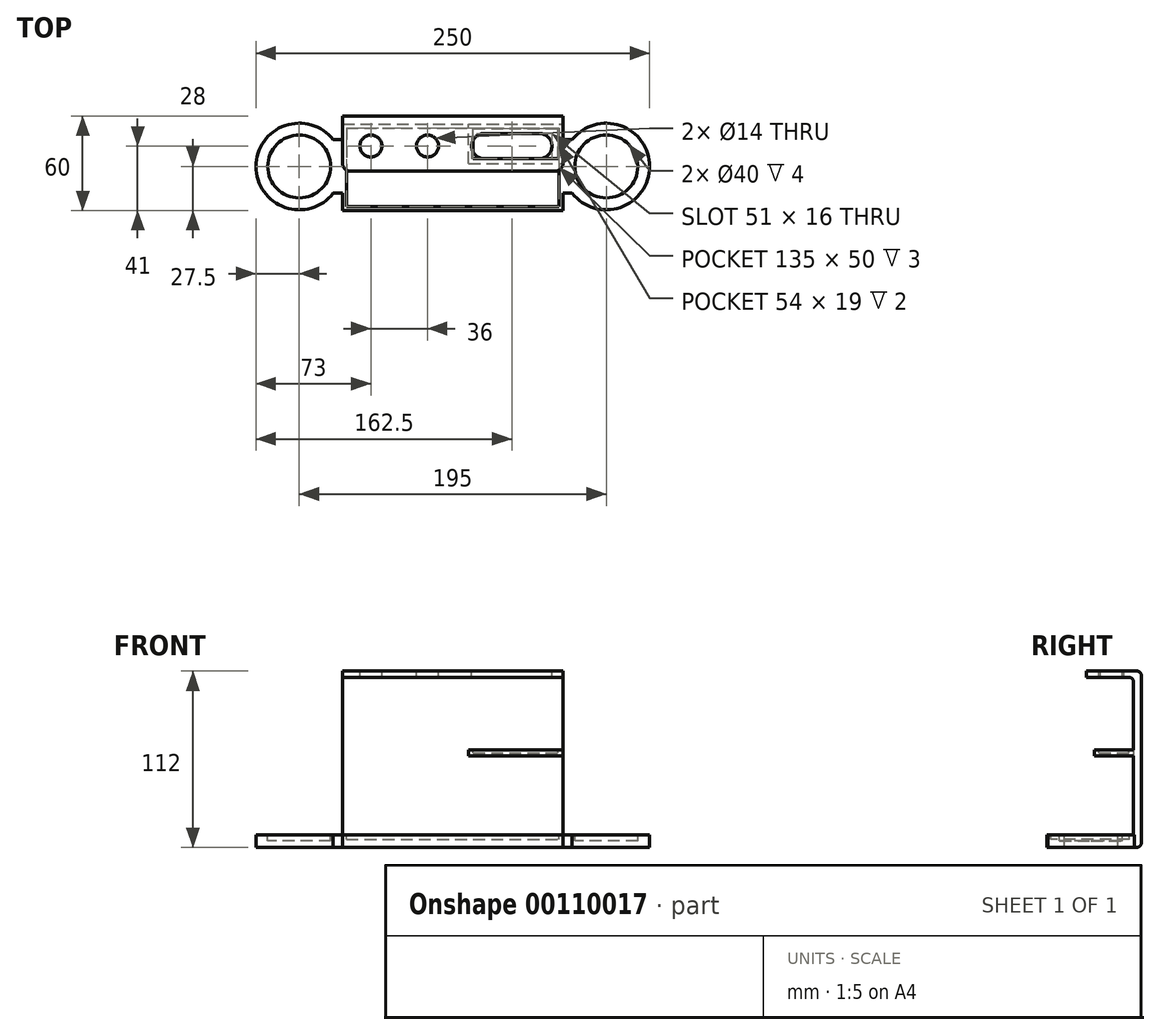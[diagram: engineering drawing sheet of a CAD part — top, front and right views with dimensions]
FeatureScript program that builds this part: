
annotation { "Feature Type Name" : "Feature", "Feature Type Description" : "" }
export const myFeature = defineFeature(function(context is Context, id is Id, definition is map)
    precondition{}
    {
        {
            var Q0;
            Q0=qCreatedBy(makeId("Right.planeOp"),FACE);
            var sketch = newSketch(context, id + "F0", { "sketchPlane" : qUnion([Q0])});
            skLineSegment(sketch, "E0", {"start": v(-85.22, 0) * mm, "end": v(92.32, 0) * mm, "construction": true});
            skLineSegment(sketch, "E1", {"start": v(0, 78) * mm, "end": v(0, -85.56) * mm, "construction": true});
            skLineSegment(sketch, "E2.right", {"start": v(0, 51) * mm, "end": v(0, -55) * mm});
            skLineSegment(sketch, "E3.top", {"start": v(-60, -50) * mm, "end": v(-5, -50) * mm});
            skLineSegment(sketch, "E3.right", {"start": v(-5, 47) * mm, "end": v(-5, -50) * mm});
            skLineSegment(sketch, "E4", {"start": v(-3, 54) * mm, "end": v(-35, 54) * mm});
            skLineSegment(sketch, "E5", {"start": v(-35, 50) * mm, "end": v(-8, 50) * mm});
            skLineSegment(sketch, "E6", {"start": v(-3, -58) * mm, "end": v(-60, -58) * mm});
            skLineSegment(sketch, "E7", {"start": v(-60, -50) * mm, "end": v(-60, -58) * mm});
            skPoint(sketch, "E8.visualSharp", {"position": v(0, 54) * mm});
            skArc(sketch, "E8.filletArc", {"start": v(0, 51) * mm, "mid": v(-0.88, 53.12) * mm, "end": v(-3, 54) * mm});
            skPoint(sketch, "E9.visualSharp", {"position": v(0, -58) * mm});
            skArc(sketch, "E9.filletArc", {"start": v(-3, -58) * mm, "mid": v(-0.88, -57.12) * mm, "end": v(0, -55) * mm});
            skPoint(sketch, "E10.visualSharp", {"position": v(-5, 50) * mm});
            skArc(sketch, "E10.filletArc", {"start": v(-5, 47) * mm, "mid": v(-5.88, 49.12) * mm, "end": v(-8, 50) * mm});
            skLineSegment(sketch, "E11", {"start": v(-35, 54) * mm, "end": v(-35, 50) * mm});
            skSolve(sketch);
        }
        {
            var Q0;
            Q0=makeQuery(id+"F0.imprint","IMPRINT",FACE,{"disambiguationData":[TD([[makeQuery(id+"F0.imprint","IMPRINT",EDGE,{"derivedFrom":sQuery(id+"F0.wireOp",EDGE,"E2.right")}),-1.0]])]});
            extrude(context, id + "F1", {"entities" : qUnion([Q0]), "oppositeDirection" : true, "depth" : 70 * mm, "hasSecondDirection" : true, "secondDirectionOppositeDirection" : false, "secondDirectionDepth" : 70 * mm});
        }
        {
            var Q0;
            Q0=makeQuery(id+"F1.opExtrude","SWEPT_FACE",FACE,{"disambiguationData":[OSD([sQuery(id+"F0.wireOp",EDGE,"E4")])]});
            var sketch = newSketch(context, id + "F2", { "sketchPlane" : qUnion([Q0])});
            skCircle(sketch, "E12", {"center": v(-52, -19) * mm, "radius": 7 * mm});
            skCircle(sketch, "E13", {"center": v(-16, -19) * mm, "radius": 7 * mm});
            skLineSegment(sketch, "E14", {"start": v(-78.22, -19) * mm, "end": v(92.14, -19) * mm, "construction": true});
            skLineSegment(sketch, "E15", {"start": v(0, 33.35) * mm, "end": v(0, -66.78) * mm, "construction": true});
            skArc(sketch, "E16", {"start": v(20, -11) * mm, "mid": v(12, -19) * mm, "end": v(20, -27) * mm});
            skArc(sketch, "E17", {"start": v(55, -27) * mm, "mid": v(63, -19) * mm, "end": v(55, -11) * mm});
            skLineSegment(sketch, "E18.bottom", {"start": v(20, -11) * mm, "end": v(55, -11) * mm});
            skLineSegment(sketch, "E18.top", {"start": v(20, -27) * mm, "end": v(55, -27) * mm});
            skSolve(sketch);
        }
        {
            var Q0;
            Q0=makeQuery(id+"F2.imprint","IMPRINT",FACE,{"disambiguationData":[TD([[makeQuery(id+"F2.imprint","IMPRINT",EDGE,{"derivedFrom":sQuery(id+"F2.wireOp",EDGE,"E16")}),1.0]])]});
            var Q1;
            Q1=makeQuery(id+"F2.imprint","IMPRINT",FACE,{"disambiguationData":[TD([[makeQuery(id+"F2.imprint","IMPRINT",EDGE,{"derivedFrom":sQuery(id+"F2.wireOp",EDGE,"E13")}),1.0]])]});
            var Q2;
            Q2=makeQuery(id+"F2.imprint","IMPRINT",FACE,{"disambiguationData":[TD([[makeQuery(id+"F2.imprint","IMPRINT",EDGE,{"derivedFrom":sQuery(id+"F2.wireOp",EDGE,"E12")}),1.0]])]});
            extrude(context, id + "F3", {"entities" : qUnion([Q0, Q1, Q2]), "operationType" : NewBodyOperationType.REMOVE, "endBound" : BoundingType.UP_TO_NEXT, "oppositeDirection" : true, "depth" : 25 * mm});
        }
        {
            var Q0;
            Q0=makeQuery(id+"F1.opExtrude","SWEPT_FACE",FACE,{"disambiguationData":[OSD([sQuery(id+"F0.wireOp",EDGE,"E3.top")])]});
            var sketch = newSketch(context, id + "F4", { "sketchPlane" : qUnion([Q0])});
            skLineSegment(sketch, "E19.bottom", {"start": v(-67.5, -7.5) * mm, "end": v(67.5, -7.5) * mm});
            skLineSegment(sketch, "E19.top", {"start": v(-67.5, -57.5) * mm, "end": v(67.5, -57.5) * mm});
            skLineSegment(sketch, "E19.left", {"start": v(-67.5, -7.5) * mm, "end": v(-67.5, -57.5) * mm});
            skLineSegment(sketch, "E19.right", {"start": v(67.5, -7.5) * mm, "end": v(67.5, -57.5) * mm});
            skSolve(sketch);
        }
        {
            var Q0;
            Q0=makeQuery(id+"F4.imprint","IMPRINT",FACE,{"disambiguationData":[TD([[makeQuery(id+"F4.imprint","IMPRINT",EDGE,{"derivedFrom":sQuery(id+"F4.wireOp",EDGE,"E19.bottom")}),-1.0]])]});
            extrude(context, id + "F5", {"entities" : qUnion([Q0]), "operationType" : NewBodyOperationType.REMOVE, "oppositeDirection" : true, "depth" : 3 * mm});
        }
        {
            var Q0;
            Q0=makeQuery(id+"F1.opExtrude","SWEPT_FACE",FACE,{"disambiguationData":[OSD([sQuery(id+"F0.wireOp",EDGE,"E3.top")])]});
            var sketch = newSketch(context, id + "F6", { "sketchPlane" : qUnion([Q0])});
            skLineSegment(sketch, "E20.bottom", {"start": v(70, -49) * mm, "end": v(75.88, -49) * mm});
            skLineSegment(sketch, "E20.top", {"start": v(70, -15) * mm, "end": v(75.88, -15) * mm});
            skLineSegment(sketch, "E20.left", {"start": v(70, -49) * mm, "end": v(70, -15) * mm});
            skCircle(sketch, "E21", {"center": v(97.5, -32) * mm, "radius": 27.5 * mm});
            skLineSegment(sketch, "E22", {"start": v(0, -71.48) * mm, "end": v(0, 11.2) * mm, "construction": true});
            skPoint(sketch, "E23.startSnap0", {"position": v(70, -32) * mm});
            skLineSegment(sketch, "E24", {"start": v(-74.48, -32) * mm, "end": v(108.38, -32) * mm, "construction": true});
            skCircle(sketch, "E25.MirrorC", {"center": v(-97.5, -32) * mm, "radius": 27.5 * mm});
            skLineSegment(sketch, "E26.MirrorCS", {"start": v(-70, -49) * mm, "end": v(-75.88, -49) * mm});
            skLineSegment(sketch, "E27.MirrorCS", {"start": v(-70, -15) * mm, "end": v(-75.88, -15) * mm});
            skLineSegment(sketch, "E28.MirrorCS", {"start": v(-70, -49) * mm, "end": v(-70, -15) * mm});
            skSolve(sketch);
        }
        {
            var Q0;
            Q0 = qSketchRegion(id + "F6", true);
            extrude(context, id + "F7", {"entities" : qUnion([Q0]), "operationType" : NewBodyOperationType.ADD, "oppositeDirection" : true, "depth" : 8 * mm});
        }
        {
            var Q0;
            Q0=makeQuery(id+"F7.boolean.opBoolean","MERGE",FACE,{"derivedFrom":[makeQuery(id+"F1.opExtrude","SWEPT_FACE",FACE,{"disambiguationData":[OSD([sQuery(id+"F0.wireOp",EDGE,"E3.top")])]}),makeQuery(id+"F7.opExtrude","CAP_FACE",FACE,{"disambiguationData":[OSD([sQuery(id+"F6.wireOp",EDGE,"E20.bottom"),sQuery(id+"F6.wireOp",EDGE,"E20.top"),sQuery(id+"F6.wireOp",EDGE,"E20.left"),sQuery(id+"F6.wireOp",EDGE,"E21")])],"isStart":true}),makeQuery(id+"F7.opExtrude","CAP_FACE",FACE,{"disambiguationData":[OSD([sQuery(id+"F6.wireOp",EDGE,"E25.MirrorC"),sQuery(id+"F6.wireOp",EDGE,"E26.MirrorCS"),sQuery(id+"F6.wireOp",EDGE,"E27.MirrorCS"),sQuery(id+"F6.wireOp",EDGE,"E28.MirrorCS")])],"isStart":true})]});
            var sketch = newSketch(context, id + "F8", { "sketchPlane" : qUnion([Q0])});
            skCircle(sketch, "E29", {"center": v(-97.5, -32) * mm, "radius": 20 * mm});
            skCircle(sketch, "E30", {"center": v(97.5, -32) * mm, "radius": 20 * mm});
            skLineSegment(sketch, "E31", {"start": v(-120.03, -32) * mm, "end": v(227.2, -32) * mm, "construction": true});
            skSolve(sketch);
        }
        {
            var Q0;
            Q0 = qSketchRegion(id + "F8", true);
            extrude(context, id + "F9", {"entities" : qUnion([Q0]), "operationType" : NewBodyOperationType.REMOVE, "oppositeDirection" : true, "depth" : 4 * mm});
        }
        {
            var Q0;
            Q0=makeQuery(id+"F1.opExtrude","SWEPT_FACE",FACE,{"disambiguationData":[OSD([sQuery(id+"F0.wireOp",EDGE,"E3.right")])]});
            var sketch = newSketch(context, id + "F10", { "sketchPlane" : qUnion([Q0])});
            skLineSegment(sketch, "E32.bottom", {"start": v(10, 4) * mm, "end": v(70, 4) * mm});
            skLineSegment(sketch, "E32.top", {"start": v(10, 0) * mm, "end": v(70, 0) * mm});
            skLineSegment(sketch, "E32.left", {"start": v(10, 4) * mm, "end": v(10, 0) * mm});
            skLineSegment(sketch, "E32.right", {"start": v(70, 4) * mm, "end": v(70, 0) * mm});
            skSolve(sketch);
        }
        {
            var Q0;
            Q0=makeQuery(id+"F10.imprint","IMPRINT",FACE,{"disambiguationData":[TD([[makeQuery(id+"F10.imprint","IMPRINT",EDGE,{"derivedFrom":sQuery(id+"F10.wireOp",EDGE,"E32.bottom")}),-1.0]])]});
            extrude(context, id + "F11", {"entities" : qUnion([Q0]), "operationType" : NewBodyOperationType.ADD, "depth" : 25 * mm});
        }
        {
            var Q0;
            Q0=makeQuery(id+"F11.opExtrude","SWEPT_FACE",FACE,{"disambiguationData":[OSD([sQuery(id+"F10.wireOp",EDGE,"E32.bottom")])]});
            var sketch = newSketch(context, id + "F12", { "sketchPlane" : qUnion([Q0])});
            skLineSegment(sketch, "E33.bottom", {"start": v(13, -27) * mm, "end": v(67, -27) * mm});
            skLineSegment(sketch, "E33.top", {"start": v(13, -8) * mm, "end": v(67, -8) * mm});
            skLineSegment(sketch, "E33.left", {"start": v(13, -27) * mm, "end": v(13, -8) * mm});
            skLineSegment(sketch, "E33.right", {"start": v(67, -27) * mm, "end": v(67, -8) * mm});
            skSolve(sketch);
        }
        {
            var Q0;
            Q0=makeQuery(id+"F12.imprint","IMPRINT",FACE,{"disambiguationData":[TD([[makeQuery(id+"F12.imprint","IMPRINT",EDGE,{"derivedFrom":sQuery(id+"F12.wireOp",EDGE,"E33.bottom")}),1.0]])]});
            extrude(context, id + "F13", {"entities" : qUnion([Q0]), "operationType" : NewBodyOperationType.REMOVE, "oppositeDirection" : true, "depth" : 2 * mm});
        }
        {
            var Q0;
            Q0=makeQuery(id+"F1.opExtrude","CAP_EDGE",EDGE,{"disambiguationData":[OSD([sQuery(id+"F0.wireOp",EDGE,"E11")])],"isStart":false});
            var Q1;
            Q1=makeQuery(id+"F1.opExtrude","CAP_EDGE",EDGE,{"disambiguationData":[OSD([sQuery(id+"F0.wireOp",EDGE,"E11")])],"isStart":true});
            fillet(context, id + "F14", {"entities" : qUnion([Q0, Q1]), "radius" : 5 * mm, "tangentPropagation" : true, "allowEdgeOverflow" : false});
        }
    });
